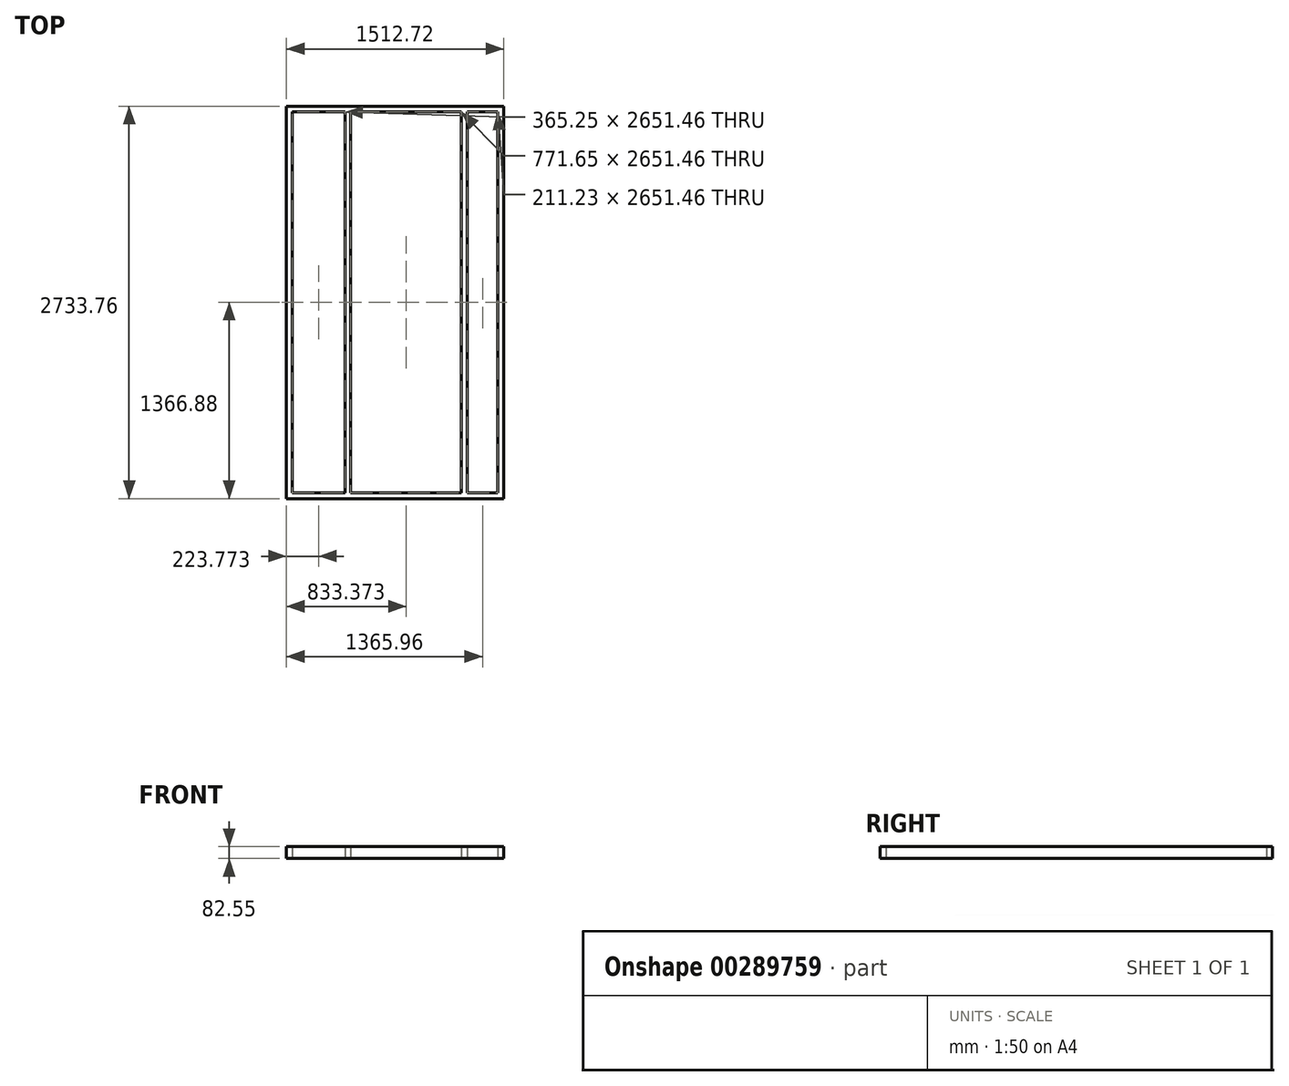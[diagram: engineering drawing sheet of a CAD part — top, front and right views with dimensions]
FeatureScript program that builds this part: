
annotation { "Feature Type Name" : "Feature", "Feature Type Description" : "" }
export const myFeature = defineFeature(function(context is Context, id is Id, definition is map)
    precondition{}
    {
        {
            var Q0;
            Q0=qCreatedBy(makeId("Top.planeOp"),FACE);
            var sketch = newSketch(context, id + "F0", { "sketchPlane" : qUnion([Q0])});
            skLineSegment(sketch, "E0.bottom", {"start": v(756.36, -1366.88) * mm, "end": v(-756.36, -1366.88) * mm});
            skLineSegment(sketch, "E0.top", {"start": v(756.36, 1366.88) * mm, "end": v(-756.36, 1366.88) * mm});
            skLineSegment(sketch, "E0.left", {"start": v(756.36, -1366.88) * mm, "end": v(756.36, 1366.88) * mm});
            skLineSegment(sketch, "E0.right", {"start": v(-756.36, -1366.88) * mm, "end": v(-756.36, 1366.88) * mm});
            skPoint(sketch, "E0.middle", {"position": v(0, 0) * mm});
            skLineSegment(sketch, "E1.bottom", {"start": v(715.21, -1325.73) * mm, "end": v(-715.21, -1325.73) * mm});
            skLineSegment(sketch, "E1.top", {"start": v(715.21, 1325.73) * mm, "end": v(-715.21, 1325.73) * mm});
            skLineSegment(sketch, "E1.left", {"start": v(715.21, -1325.73) * mm, "end": v(715.21, 1325.73) * mm});
            skLineSegment(sketch, "E1.right", {"start": v(-715.21, -1325.73) * mm, "end": v(-715.21, 1325.73) * mm});
            skLineSegment(sketch, "E2.right", {"start": v(-308.81, -1325.73) * mm, "end": v(-308.81, 1325.73) * mm});
            skLineSegment(sketch, "E3", {"start": v(-349.96, 1325.73) * mm, "end": v(-349.96, -1325.73) * mm});
            skLineSegment(sketch, "E4.bottom", {"start": v(56.44, 1325.73) * mm, "end": v(97.59, 1325.73) * mm});
            skLineSegment(sketch, "E4.top", {"start": v(56.44, -1325.73) * mm, "end": v(97.59, -1325.73) * mm});
            skLineSegment(sketch, "E4.left", {"start": v(56.44, 1325.73) * mm, "end": v(56.44, -1325.73) * mm});
            skLineSegment(sketch, "E4.right", {"start": v(97.59, 1325.73) * mm, "end": v(97.59, -1325.73) * mm});
            skLineSegment(sketch, "E5", {"start": v(77.01, 1325.73) * mm, "end": v(77.01, -1325.73) * mm, "construction": true});
            skLineSegment(sketch, "E6.MirrorCS", {"start": v(462.84, -1325.73) * mm, "end": v(462.84, 1325.73) * mm});
            skLineSegment(sketch, "E7.MirrorCS", {"start": v(503.99, 1325.73) * mm, "end": v(503.99, -1325.73) * mm});
            skLineSegment(sketch, "E8", {"start": v(442.26, 1325.73) * mm, "end": v(442.26, -1325.73) * mm, "construction": true});
            skLineSegment(sketch, "E9.MirrorCS", {"start": v(786.94, 1325.73) * mm, "end": v(786.94, -1325.73) * mm});
            skLineSegment(sketch, "E10.MirrorCS", {"start": v(828.1, 1325.73) * mm, "end": v(828.1, -1325.73) * mm});
            skSolve(sketch);
        }
        {
            var Q0;
            Q0=makeQuery(id+"F0.imprint","IMPRINT",FACE,{"disambiguationData":[TD([[makeQuery(id+"F0.imprint","IMPRINT",EDGE,{"derivedFrom":sQuery(id+"F0.wireOp",EDGE,"E0.bottom")}),-1.0]])]});
            var Q1;
            {var subQ6=sQuery(id+"F0.wireOp",EDGE,"E3");Q1=makeQuery(id+"F0.imprint","IMPRINT",FACE,{"disambiguationData":[TD([[makeQuery(id+"F0.imprint","IMPRINT",EDGE,{"derivedFrom":subQ6}),1.0]])]});}
            var Q2;
            {var subQ0=sQuery(id+"F0.wireOp",EDGE,"E2.top");var subQ1=sQuery(id+"F0.wireOp",EDGE,"CeLBKzQn-vrWp-3Gcy-STSl-m5YtVVHxxhsw.right");var subQ2=makeQuery(id+"F0.imprint","INTERSECT",VERTEX,{"derivedFrom":[subQ1,subQ0]});Q2=makeQuery(id+"F0.imprint","IMPRINT",FACE,{"disambiguationData":[TD([[makeQuery(id+"F0.imprint","IMPRINT",EDGE,{"disambiguationData":[TD([[subQ2,1.0]])],"derivedFrom":subQ1}),1.0]])]});}
            var Q3;
            {var subQ0=sQuery(id+"F0.wireOp",EDGE,"2T1vTNZ0-FRP3-QXiO-6JWe-jevLZosKjYpy.bottom");Q3=makeQuery(id+"F0.imprint","IMPRINT",FACE,{"disambiguationData":[TD([[makeQuery(id+"F0.imprint","IMPRINT",EDGE,{"derivedFrom":subQ0}),-1.0]])]});}
            var Q4;
            {var subQ0=sQuery(id+"F0.wireOp",EDGE,"eAwVO68b-qbLe-tcLK-FJkz-neVmvZHEHzhS");Q4=makeQuery(id+"F0.imprint","IMPRINT",FACE,{"disambiguationData":[TD([[makeQuery(id+"F0.imprint","IMPRINT",EDGE,{"derivedFrom":subQ0}),1.0]])]});}
            var Q5;
            {var subQ3=sQuery(id+"F0.wireOp",EDGE,"eAwVO68b-qbLe-tcLK-FJkz-neVmvZHEHzhS");Q5=makeQuery(id+"F0.imprint","IMPRINT",FACE,{"disambiguationData":[TD([[makeQuery(id+"F0.imprint","IMPRINT",EDGE,{"derivedFrom":subQ3}),-1.0]])]});}
            var Q6;
            Q6=makeQuery(id+"F0.imprint","IMPRINT",FACE,{"disambiguationData":[TD([[makeQuery(id+"F0.imprint","IMPRINT",EDGE,{"derivedFrom":sQuery(id+"F0.wireOp",EDGE,"2T1vTNZ0-FRP3-QXiO-6JWe-jevLZosKjYpy.bottom")}),1.0]])]});
            var Q7;
            {var subQ0=sQuery(id+"F0.wireOp",EDGE,"E2.top");var subQ1=sQuery(id+"F0.wireOp",EDGE,"CeLBKzQn-vrWp-3Gcy-STSl-m5YtVVHxxhsw.left");var subQ2=makeQuery(id+"F0.imprint","INTERSECT",VERTEX,{"derivedFrom":[subQ1,subQ0]});Q7=makeQuery(id+"F0.imprint","IMPRINT",FACE,{"disambiguationData":[TD([[makeQuery(id+"F0.imprint","IMPRINT",EDGE,{"disambiguationData":[TD([[subQ2,1.0]])],"derivedFrom":subQ1}),-1.0]])]});}
            var Q8;
            {var subQ5=sQuery(id+"F0.wireOp",EDGE,"RKO7VibA-5L9s-bFsq-QhT8-NU87CP0l9bWE");Q8=makeQuery(id+"F0.imprint","IMPRINT",FACE,{"disambiguationData":[TD([[makeQuery(id+"F0.imprint","IMPRINT",EDGE,{"derivedFrom":subQ5}),-1.0]])]});}
            var Q9;
            {var subQ0=sQuery(id+"F0.wireOp",EDGE,"eimdUF1S-VLgt-R7h1-7aaf-AqgagJHAWkX2");var subQ1=sQuery(id+"F0.wireOp",EDGE,"CeLBKzQn-vrWp-3Gcy-STSl-m5YtVVHxxhsw.left");var subQ2=makeQuery(id+"F0.imprint","INTERSECT",VERTEX,{"derivedFrom":[subQ1,subQ0]});Q9=makeQuery(id+"F0.imprint","IMPRINT",FACE,{"disambiguationData":[TD([[makeQuery(id+"F0.imprint","IMPRINT",EDGE,{"disambiguationData":[TD([[subQ2,-1.0]])],"derivedFrom":subQ1}),-1.0]])]});}
            var Q10;
            {var subQ0=sQuery(id+"F0.wireOp",EDGE,"E2.bottom");var subQ1=sQuery(id+"F0.wireOp",EDGE,"CeLBKzQn-vrWp-3Gcy-STSl-m5YtVVHxxhsw.left");var subQ2=makeQuery(id+"F0.imprint","INTERSECT",VERTEX,{"derivedFrom":[subQ1,subQ0]});Q10=makeQuery(id+"F0.imprint","IMPRINT",FACE,{"disambiguationData":[TD([[makeQuery(id+"F0.imprint","IMPRINT",EDGE,{"disambiguationData":[TD([[subQ2,-1.0]])],"derivedFrom":subQ1}),-1.0]])]});}
            var Q11;
            {var subQ0=sQuery(id+"F0.wireOp",EDGE,"E6.MirrorCS");Q11=makeQuery(id+"F0.imprint","IMPRINT",FACE,{"disambiguationData":[TD([[makeQuery(id+"F0.imprint","IMPRINT",EDGE,{"derivedFrom":subQ0}),-1.0]])]});}
            var Q12;
            {var subQ0=sQuery(id+"F0.wireOp",EDGE,"E9.MirrorCS");Q12=makeQuery(id+"F0.imprint","IMPRINT",FACE,{"disambiguationData":[TD([[makeQuery(id+"F0.imprint","IMPRINT",EDGE,{"derivedFrom":subQ0}),1.0]])]});}
            var Q13;
            Q13=makeQuery(id+"F0.imprint","IMPRINT",FACE,{"disambiguationData":[TD([[makeQuery(id+"F0.imprint","IMPRINT",EDGE,{"derivedFrom":sQuery(id+"F0.wireOp",EDGE,"E4.bottom")}),-1.0]])]});
            extrude(context, id + "F1", {"entities" : qUnion([Q0, Q1, Q2, Q3, Q4, Q5, Q6, Q7, Q8, Q9, Q10, Q11, Q12, Q13]), "depth" : 82.55 * mm});
        }
    });
